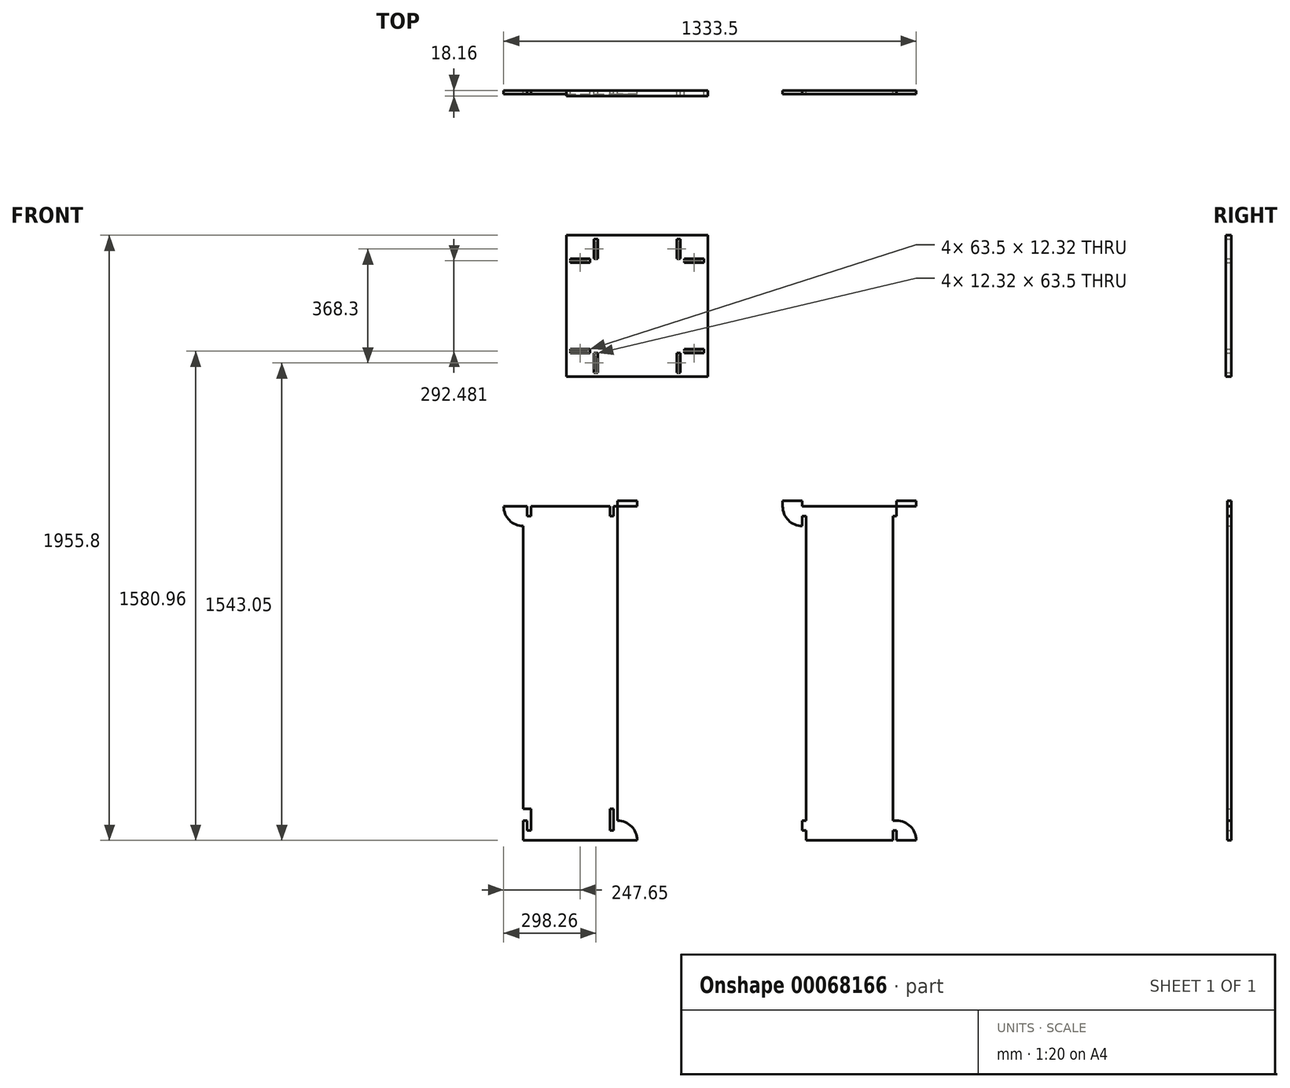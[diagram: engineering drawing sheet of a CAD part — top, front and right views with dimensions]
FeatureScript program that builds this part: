
annotation { "Feature Type Name" : "Feature", "Feature Type Description" : "" }
export const myFeature = defineFeature(function(context is Context, id is Id, definition is map)
    precondition{}
    {
        {
            var Q0;
            Q0=qCreatedBy(makeId("Front.planeOp"),FACE);
            var sketch = newSketch(context, id + "F0", { "sketchPlane" : qUnion([Q0])});
            skLineSegment(sketch, "E0.bottom", {"start": v(-139.7, 596.9) * mm, "end": v(165.1, 596.9) * mm});
            skLineSegment(sketch, "E0.top", {"start": v(-139.7, -482.6) * mm, "end": v(165.1, -482.6) * mm});
            skLineSegment(sketch, "E0.left", {"start": v(-139.7, 596.9) * mm, "end": v(-139.7, -482.6) * mm});
            skLineSegment(sketch, "E0.right", {"start": v(165.1, 596.9) * mm, "end": v(165.1, -482.6) * mm});
            skArc(sketch, "E1", {"start": v(-203.2, 596.9) * mm, "mid": v(-184.6, 552) * mm, "end": v(-139.7, 533.4) * mm});
            skLineSegment(sketch, "E2", {"start": v(-139.7, 596.9) * mm, "end": v(-203.2, 596.9) * mm, "construction": true});
            skLineSegment(sketch, "E3.bottom", {"start": v(-215.9, 596.9) * mm, "end": v(241.3, 596.9) * mm});
            skLineSegment(sketch, "E3.top", {"start": v(-215.9, 635) * mm, "end": v(241.3, 635) * mm, "construction": true});
            skLineSegment(sketch, "E3.left", {"start": v(-215.9, 596.9) * mm, "end": v(-215.9, 635) * mm, "construction": true});
            skLineSegment(sketch, "E4", {"start": v(12.7, 596.9) * mm, "end": v(12.7, -482.6) * mm, "construction": true});
            skLineSegment(sketch, "E5.MirrorCS", {"start": v(165.1, 596.9) * mm, "end": v(228.6, 596.9) * mm, "construction": true});
            skLineSegment(sketch, "E6.MirrorCS", {"start": v(241.3, 596.9) * mm, "end": v(241.3, 635) * mm, "construction": true});
            skArc(sketch, "E7.MirrorCS", {"start": v(228.6, 596.9) * mm, "mid": v(210, 552) * mm, "end": v(165.1, 533.4) * mm});
            skLineSegment(sketch, "E8", {"start": v(165.1, 57.15) * mm, "end": v(-139.7, 57.15) * mm, "construction": true});
            skArc(sketch, "E9.MirrorCS", {"start": v(-203.2, -482.6) * mm, "mid": v(-184.6, -437.7) * mm, "end": v(-139.7, -419.1) * mm});
            skArc(sketch, "E10.MirrorCS", {"start": v(228.6, -482.6) * mm, "mid": v(210, -437.7) * mm, "end": v(165.1, -419.1) * mm});
            skLineSegment(sketch, "E11", {"start": v(-139.7, -482.6) * mm, "end": v(-203.2, -482.6) * mm});
            skLineSegment(sketch, "E12", {"start": v(165.1, -482.6) * mm, "end": v(228.6, -482.6) * mm});
            skLineSegment(sketch, "E13.bottom", {"start": v(-203.2, 596.9) * mm, "end": v(-139.7, 596.9) * mm});
            skLineSegment(sketch, "E13.top", {"start": v(-203.2, 614.68) * mm, "end": v(-139.7, 614.68) * mm});
            skLineSegment(sketch, "E13.left", {"start": v(-203.2, 596.9) * mm, "end": v(-203.2, 614.68) * mm});
            skLineSegment(sketch, "E13.right", {"start": v(-139.7, 596.9) * mm, "end": v(-139.7, 614.68) * mm});
            skLineSegment(sketch, "E14.MirrorCS", {"start": v(228.6, 596.9) * mm, "end": v(228.6, 614.68) * mm});
            skLineSegment(sketch, "E15.MirrorCS", {"start": v(228.6, 614.68) * mm, "end": v(165.1, 614.68) * mm});
            skLineSegment(sketch, "E16.MirrorCS", {"start": v(165.1, 596.9) * mm, "end": v(165.1, 614.68) * mm});
            skLineSegment(sketch, "E17.bottom", {"start": v(0, 1473.2) * mm, "end": v(457.2, 1473.2) * mm});
            skLineSegment(sketch, "E17.top", {"start": v(0, 1016) * mm, "end": v(457.2, 1016) * mm});
            skLineSegment(sketch, "E17.left", {"start": v(0, 1473.2) * mm, "end": v(0, 1016) * mm});
            skLineSegment(sketch, "E17.right", {"start": v(457.2, 1473.2) * mm, "end": v(457.2, 1016) * mm});
            skLineSegment(sketch, "E18.bottom", {"start": v(12.7, 1092.2) * mm, "end": v(76.2, 1092.2) * mm});
            skLineSegment(sketch, "E18.top", {"start": v(12.7, 1104.52) * mm, "end": v(76.2, 1104.52) * mm});
            skLineSegment(sketch, "E18.left", {"start": v(12.7, 1092.2) * mm, "end": v(12.7, 1104.52) * mm});
            skLineSegment(sketch, "E18.right", {"start": v(76.2, 1092.2) * mm, "end": v(76.2, 1104.52) * mm});
            skLineSegment(sketch, "E19", {"start": v(228.6, 1473.2) * mm, "end": v(228.6, 1016) * mm, "construction": true});
            skLineSegment(sketch, "E20", {"start": v(0, 1244.6) * mm, "end": v(457.2, 1244.6) * mm, "construction": true});
            skLineSegment(sketch, "E21.MirrorCS", {"start": v(444.5, 1092.2) * mm, "end": v(444.5, 1104.52) * mm});
            skLineSegment(sketch, "E22.MirrorCS", {"start": v(381, 1092.2) * mm, "end": v(381, 1104.52) * mm});
            skLineSegment(sketch, "E23.MirrorCS", {"start": v(444.5, 1092.2) * mm, "end": v(381, 1092.2) * mm});
            skLineSegment(sketch, "E24.MirrorCS", {"start": v(444.5, 1104.52) * mm, "end": v(381, 1104.52) * mm});
            skLineSegment(sketch, "E25.MirrorCS", {"start": v(444.5, 1397) * mm, "end": v(444.5, 1384.68) * mm});
            skLineSegment(sketch, "E26.MirrorCS", {"start": v(381, 1397) * mm, "end": v(381, 1384.68) * mm});
            skLineSegment(sketch, "E27.MirrorCS", {"start": v(76.2, 1397) * mm, "end": v(76.2, 1384.68) * mm});
            skLineSegment(sketch, "E28.MirrorCS", {"start": v(12.7, 1397) * mm, "end": v(12.7, 1384.68) * mm});
            skLineSegment(sketch, "E29.MirrorCS", {"start": v(444.5, 1397) * mm, "end": v(381, 1397) * mm});
            skLineSegment(sketch, "E30.MirrorCS", {"start": v(12.7, 1397) * mm, "end": v(76.2, 1397) * mm});
            skLineSegment(sketch, "E31.MirrorCS", {"start": v(444.5, 1384.68) * mm, "end": v(381, 1384.68) * mm});
            skLineSegment(sketch, "E32.MirrorCS", {"start": v(12.7, 1384.68) * mm, "end": v(76.2, 1384.68) * mm});
            skLineSegment(sketch, "E33.bottom", {"start": v(88.9, 1028.7) * mm, "end": v(101.22, 1028.7) * mm});
            skLineSegment(sketch, "E33.top", {"start": v(88.9, 1092.2) * mm, "end": v(101.22, 1092.2) * mm});
            skLineSegment(sketch, "E33.left", {"start": v(88.9, 1028.7) * mm, "end": v(88.9, 1092.2) * mm});
            skLineSegment(sketch, "E33.right", {"start": v(101.22, 1028.7) * mm, "end": v(101.22, 1092.2) * mm});
            skLineSegment(sketch, "E34.MirrorCS", {"start": v(368.3, 1028.7) * mm, "end": v(355.98, 1028.7) * mm});
            skLineSegment(sketch, "E35.MirrorCS", {"start": v(355.98, 1028.7) * mm, "end": v(355.98, 1092.2) * mm});
            skLineSegment(sketch, "E36.MirrorCS", {"start": v(368.3, 1028.7) * mm, "end": v(368.3, 1092.2) * mm});
            skLineSegment(sketch, "E37.MirrorCS", {"start": v(368.3, 1092.2) * mm, "end": v(355.98, 1092.2) * mm});
            skLineSegment(sketch, "E38.MirrorCS", {"start": v(368.3, 1460.5) * mm, "end": v(355.98, 1460.5) * mm});
            skLineSegment(sketch, "E39.MirrorCS", {"start": v(368.3, 1397) * mm, "end": v(355.98, 1397) * mm});
            skLineSegment(sketch, "E40.MirrorCS", {"start": v(88.9, 1460.5) * mm, "end": v(88.9, 1397) * mm});
            skLineSegment(sketch, "E41.MirrorCS", {"start": v(88.9, 1460.5) * mm, "end": v(101.22, 1460.5) * mm});
            skLineSegment(sketch, "E42.MirrorCS", {"start": v(355.98, 1460.5) * mm, "end": v(355.98, 1397) * mm});
            skLineSegment(sketch, "E43.MirrorCS", {"start": v(368.3, 1460.5) * mm, "end": v(368.3, 1397) * mm});
            skLineSegment(sketch, "E44.MirrorCS", {"start": v(101.22, 1460.5) * mm, "end": v(101.22, 1397) * mm});
            skLineSegment(sketch, "E45.MirrorCS", {"start": v(88.9, 1397) * mm, "end": v(101.22, 1397) * mm});
            skLineSegment(sketch, "E46.top", {"start": v(762, -482.6) * mm, "end": v(1066.8, -482.6) * mm});
            skLineSegment(sketch, "E46.left", {"start": v(762, 596.9) * mm, "end": v(762, 565.15) * mm});
            skLineSegment(sketch, "E46.right", {"start": v(1066.8, 596.9) * mm, "end": v(1066.8, -482.6) * mm});
            skLineSegment(sketch, "E47", {"start": v(914.4, 596.9) * mm, "end": v(914.4, -482.6) * mm, "construction": true});
            skArc(sketch, "E48.MirrorCS", {"start": v(1130.3, -482.6) * mm, "mid": v(1111.7, -437.7) * mm, "end": v(1066.8, -419.1) * mm});
            skArc(sketch, "E49", {"start": v(698.5, 596.9) * mm, "mid": v(717.1, 552) * mm, "end": v(762, 533.4) * mm});
            skLineSegment(sketch, "E50.top", {"start": v(685.8, 635) * mm, "end": v(1143, 635) * mm, "construction": true});
            skLineSegment(sketch, "E50.bottom", {"start": v(685.8, 596.9) * mm, "end": v(1143, 596.9) * mm});
            skArc(sketch, "E51.MirrorCS", {"start": v(1130.3, 596.9) * mm, "mid": v(1111.7, 552) * mm, "end": v(1066.8, 533.4) * mm});
            skArc(sketch, "E52.MirrorCS", {"start": v(698.5, -482.6) * mm, "mid": v(717.1, -437.7) * mm, "end": v(762, -419.1) * mm});
            skLineSegment(sketch, "E46.bottom", {"start": v(762, 596.9) * mm, "end": v(1066.8, 596.9) * mm});
            skLineSegment(sketch, "E53", {"start": v(762, -482.6) * mm, "end": v(698.5, -482.6) * mm});
            skLineSegment(sketch, "E54", {"start": v(1066.8, -482.6) * mm, "end": v(1130.3, -482.6) * mm});
            skLineSegment(sketch, "E55.MirrorCS", {"start": v(1130.3, 596.9) * mm, "end": v(1130.3, 614.68) * mm});
            skLineSegment(sketch, "E56.left", {"start": v(698.5, 596.9) * mm, "end": v(698.5, 614.68) * mm});
            skLineSegment(sketch, "E57.MirrorCS", {"start": v(1066.8, 596.9) * mm, "end": v(1066.8, 614.68) * mm});
            skLineSegment(sketch, "E56.top", {"start": v(698.5, 614.68) * mm, "end": v(762, 614.68) * mm});
            skLineSegment(sketch, "E56.bottom", {"start": v(698.5, 596.9) * mm, "end": v(762, 596.9) * mm});
            skLineSegment(sketch, "E58.MirrorCS", {"start": v(1143, 596.9) * mm, "end": v(1143, 635) * mm, "construction": true});
            skLineSegment(sketch, "E59.MirrorCS", {"start": v(1066.8, 596.9) * mm, "end": v(1130.3, 596.9) * mm, "construction": true});
            skLineSegment(sketch, "E50.left", {"start": v(685.8, 596.9) * mm, "end": v(685.8, 635) * mm, "construction": true});
            skLineSegment(sketch, "E60.MirrorCS", {"start": v(1130.3, 614.68) * mm, "end": v(1066.8, 614.68) * mm});
            skLineSegment(sketch, "E61", {"start": v(762, 596.9) * mm, "end": v(698.5, 596.9) * mm, "construction": true});
            skLineSegment(sketch, "E56.right", {"start": v(762, 596.9) * mm, "end": v(762, 614.68) * mm});
            skLineSegment(sketch, "E62.bottom", {"start": v(-127, -450.85) * mm, "end": v(-114.68, -450.85) * mm});
            skLineSegment(sketch, "E62.top", {"start": v(-139.7, -381) * mm, "end": v(-114.68, -381) * mm});
            skLineSegment(sketch, "E62.left", {"start": v(-139.7, -419.1) * mm, "end": v(-139.7, -381) * mm});
            skLineSegment(sketch, "E62.right", {"start": v(-114.68, -450.85) * mm, "end": v(-114.68, -381) * mm});
            skLineSegment(sketch, "E63.top", {"start": v(-127, 565.15) * mm, "end": v(-114.68, 565.15) * mm});
            skLineSegment(sketch, "E64.top", {"start": v(-139.7, 596.9) * mm, "end": v(-114.68, 596.9) * mm});
            skLineSegment(sketch, "E64.left", {"start": v(-139.7, 565.15) * mm, "end": v(-139.7, 596.9) * mm});
            skLineSegment(sketch, "E64.right", {"start": v(-114.68, 565.15) * mm, "end": v(-114.68, 596.9) * mm});
            skLineSegment(sketch, "E65.0", {"start": v(1054.48, 533.4) * mm, "end": v(1054.48, -419.1) * mm});
            skLineSegment(sketch, "E66.0", {"start": v(774.32, 533.4) * mm, "end": v(774.32, -419.1) * mm});
            skLineSegment(sketch, "E67", {"start": v(1066.8, 533.4) * mm, "end": v(1054.48, 533.4) * mm});
            skLineSegment(sketch, "E68.bottom", {"start": v(762, 533.4) * mm, "end": v(774.32, 533.4) * mm});
            skLineSegment(sketch, "E68.top", {"start": v(762, 565.15) * mm, "end": v(774.32, 565.15) * mm});
            skLineSegment(sketch, "E68.right", {"start": v(774.32, 533.4) * mm, "end": v(774.32, 565.15) * mm});
            skLineSegment(sketch, "E69.trimOffspring", {"start": v(762, 533.4) * mm, "end": v(762, -482.6) * mm});
            skLineSegment(sketch, "E70.MirrorCS", {"start": v(1066.8, 565.15) * mm, "end": v(1054.48, 565.15) * mm});
            skLineSegment(sketch, "E71.MirrorCS", {"start": v(1054.48, 533.4) * mm, "end": v(1054.48, 565.15) * mm});
            skLineSegment(sketch, "E72.MirrorCS", {"start": v(762, -450.85) * mm, "end": v(774.32, -450.85) * mm});
            skLineSegment(sketch, "E73.MirrorCS", {"start": v(1066.8, -450.85) * mm, "end": v(1054.48, -450.85) * mm});
            skLineSegment(sketch, "E74", {"start": v(762, 565.15) * mm, "end": v(762, 533.4) * mm});
            skLineSegment(sketch, "E75", {"start": v(774.32, -450.85) * mm, "end": v(774.32, -482.6) * mm});
            skLineSegment(sketch, "E76", {"start": v(1054.48, -450.85) * mm, "end": v(1054.48, -482.6) * mm});
            skLineSegment(sketch, "E77", {"start": v(762, -419.1) * mm, "end": v(774.32, -419.1) * mm});
            skLineSegment(sketch, "E78", {"start": v(1066.8, -419.1) * mm, "end": v(1054.48, -419.1) * mm});
            skLineSegment(sketch, "E79", {"start": v(-139.7, -419.1) * mm, "end": v(-127, -419.1) * mm});
            skLineSegment(sketch, "E80", {"start": v(-127, -419.1) * mm, "end": v(-127, -450.85) * mm});
            skPoint(sketch, "E81.orphan", {"position": v(-139.7, -450.85) * mm});
            skLineSegment(sketch, "E82.MirrorCS", {"start": v(165.1, -419.1) * mm, "end": v(152.4, -419.1) * mm});
            skLineSegment(sketch, "E83.MirrorCS", {"start": v(140.08, -450.85) * mm, "end": v(140.08, -381) * mm});
            skLineSegment(sketch, "E84.MirrorCS", {"start": v(165.1, -381) * mm, "end": v(140.08, -381) * mm});
            skLineSegment(sketch, "E85.MirrorCS", {"start": v(152.4, -419.1) * mm, "end": v(152.4, -450.85) * mm});
            skLineSegment(sketch, "E86.MirrorCS", {"start": v(152.4, -450.85) * mm, "end": v(140.08, -450.85) * mm});
            skPoint(sketch, "E87.MirrorP", {"position": v(165.1, -450.85) * mm});
            skLineSegment(sketch, "E88.0", {"start": v(-127, 565.15) * mm, "end": v(-127, 596.9) * mm});
            skLineSegment(sketch, "E89.MirrorCS", {"start": v(152.4, 565.15) * mm, "end": v(140.08, 565.15) * mm});
            skLineSegment(sketch, "E90.MirrorCS", {"start": v(152.4, 565.15) * mm, "end": v(152.4, 596.9) * mm});
            skLineSegment(sketch, "E91.MirrorCS", {"start": v(140.08, 565.15) * mm, "end": v(140.08, 596.9) * mm});
            skLineSegment(sketch, "E92", {"start": v(-127, -419.1) * mm, "end": v(-127, -381) * mm});
            skLineSegment(sketch, "E93", {"start": v(152.4, -419.1) * mm, "end": v(152.4, -381) * mm});
            skSolve(sketch);
        }
        {
            var Q0;
            {var subQ2=sQuery(id+"F0.wireOp",EDGE,"E1");Q0=makeQuery(id+"F0.imprint","IMPRINT",FACE,{"disambiguationData":[TD([[makeQuery(id+"F0.imprint","IMPRINT",EDGE,{"derivedFrom":subQ2}),1.0]])]});}
            var Q1;
            {var subQ4=sQuery(id+"F0.wireOp",EDGE,"E7.MirrorCS");Q1=makeQuery(id+"F0.imprint","IMPRINT",FACE,{"disambiguationData":[TD([[makeQuery(id+"F0.imprint","IMPRINT",EDGE,{"derivedFrom":subQ4}),-1.0]])]});}
            var Q2;
            {var subQ4=sQuery(id+"F0.wireOp",EDGE,"E9.MirrorCS");Q2=makeQuery(id+"F0.imprint","IMPRINT",FACE,{"disambiguationData":[TD([[makeQuery(id+"F0.imprint","IMPRINT",EDGE,{"derivedFrom":subQ4}),-1.0]])]});}
            var Q3;
            {var subQ0=sQuery(id+"F0.wireOp",EDGE,"E10.MirrorCS");Q3=makeQuery(id+"F0.imprint","IMPRINT",FACE,{"disambiguationData":[TD([[makeQuery(id+"F0.imprint","IMPRINT",EDGE,{"derivedFrom":subQ0}),1.0]])]});}
            var Q4;
            Q4=makeQuery(id+"F0.imprint","IMPRINT",FACE,{"disambiguationData":[TD([[makeQuery(id+"F0.imprint","IMPRINT",EDGE,{"derivedFrom":sQuery(id+"F0.wireOp",EDGE,"E13.bottom")}),1.0]])]});
            var Q5;
            {var subQ2=sQuery(id+"F0.wireOp",EDGE,"E14.MirrorCS");Q5=makeQuery(id+"F0.imprint","IMPRINT",FACE,{"disambiguationData":[TD([[makeQuery(id+"F0.imprint","IMPRINT",EDGE,{"derivedFrom":subQ2}),1.0]])]});}
            var Q6;
            Q6=makeQuery(id+"F0.imprint","IMPRINT",FACE,{"disambiguationData":[TD([[makeQuery(id+"F0.imprint","IMPRINT",EDGE,{"derivedFrom":sQuery(id+"F0.wireOp",EDGE,"E56.left")}),-1.0]])]});
            var Q7;
            Q7=makeQuery(id+"F0.imprint","IMPRINT",FACE,{"disambiguationData":[TD([[makeQuery(id+"F0.imprint","IMPRINT",EDGE,{"derivedFrom":sQuery(id+"F0.wireOp",EDGE,"E46.left")}),-1.0]])]});
            var Q8;
            {var subQ2=sQuery(id+"F0.wireOp",EDGE,"E55.MirrorCS");Q8=makeQuery(id+"F0.imprint","IMPRINT",FACE,{"disambiguationData":[TD([[makeQuery(id+"F0.imprint","IMPRINT",EDGE,{"derivedFrom":subQ2}),1.0]])]});}
            var Q9;
            {var subQ4=sQuery(id+"F0.wireOp",EDGE,"E51.MirrorCS");Q9=makeQuery(id+"F0.imprint","IMPRINT",FACE,{"disambiguationData":[TD([[makeQuery(id+"F0.imprint","IMPRINT",EDGE,{"derivedFrom":subQ4}),-1.0]])]});}
            var Q10;
            {var subQ0=sQuery(id+"F0.wireOp",EDGE,"E52.MirrorCS");Q10=makeQuery(id+"F0.imprint","IMPRINT",FACE,{"disambiguationData":[TD([[makeQuery(id+"F0.imprint","IMPRINT",EDGE,{"derivedFrom":subQ0}),-1.0]])]});}
            var Q11;
            {var subQ0=sQuery(id+"F0.wireOp",EDGE,"E48.MirrorCS");Q11=makeQuery(id+"F0.imprint","IMPRINT",FACE,{"disambiguationData":[TD([[makeQuery(id+"F0.imprint","IMPRINT",EDGE,{"derivedFrom":subQ0}),1.0]])]});}
            var Q12;
            {var subQ8=sQuery(id+"F0.wireOp",EDGE,"E0.top");Q12=makeQuery(id+"F0.imprint","IMPRINT",FACE,{"disambiguationData":[TD([[makeQuery(id+"F0.imprint","IMPRINT",EDGE,{"derivedFrom":subQ8}),1.0]])]});}
            var Q13;
            Q13=makeQuery(id+"F0.imprint","IMPRINT",FACE,{"disambiguationData":[TD([[makeQuery(id+"F0.imprint","IMPRINT",EDGE,{"derivedFrom":sQuery(id+"F0.wireOp",EDGE,"E46.left")}),1.0]])]});
            var Q14;
            {var subQ0=sQuery(id+"F0.wireOp",EDGE,"E62.left");Q14=makeQuery(id+"F0.imprint","IMPRINT",FACE,{"disambiguationData":[TD([[makeQuery(id+"F0.imprint","IMPRINT",EDGE,{"derivedFrom":subQ0}),-1.0]])]});}
            var Q15;
            {var subQ0=sQuery(id+"F0.wireOp",EDGE,"E82.MirrorCS");Q15=makeQuery(id+"F0.imprint","IMPRINT",FACE,{"disambiguationData":[TD([[makeQuery(id+"F0.imprint","IMPRINT",EDGE,{"derivedFrom":subQ0}),-1.0]])]});}
            extrude(context, id + "F1", {"entities" : qUnion([Q0, Q1, Q2, Q3, Q4, Q5, Q6, Q7, Q8, Q9, Q10, Q11, Q12, Q13, Q14, Q15]), "depth" : 12.32 * mm});
        }
        {
            var Q0;
            Q0=makeQuery(id+"F0.imprint","IMPRINT",FACE,{"disambiguationData":[TD([[makeQuery(id+"F0.imprint","IMPRINT",EDGE,{"derivedFrom":sQuery(id+"F0.wireOp",EDGE,"E17.bottom")}),-1.0]])]});
            extrude(context, id + "F2", {"entities" : qUnion([Q0]), "depth" : 18.16 * mm});
        }
    });
